# Revit family: LAMP_FIL 70 CORNER OPAL RECESSED
name_source: partatom
category: Luminarias
revit_build: Autodesk Revit 2015 (Build: 20140606_1530(x64)
units: mm (PartAtom-declared; Revit-internal decimal feet)

## types (8) — shared parameters
CRI = 80
Cambio de temperatura de color de luz atenuada = <Ninguno>
Comentarios de tipo = Availability of switching between accessories through visibility parameters when placed in a project.
Dimensions = (303 x 368) x 89 x 70 mm
Fabricante = LAMP
Filtro de color = 16777215
Gear = Electronic
IEE = A++
IFC Clasificación = Light Fixture
Installation instructions = https://www.lamp.es
Insulation class = I
LED Lifetime = 50000 L80 B10
Last update = 12/08/2020
Longitud de línea de emisión = 300 mm
Luminaire type = Indoor - Modular System
Lámpara = LED MID-POWER
MacAdam = 3
Manufacturer URL = http://www.lamp.es
Manufacturer country = Spain
Manufacturer name = LAMP
Material Difusor = LAMP_PC Difusor Opal Fil
Model explanation = Availability of switching between accessories through visibility parameters when placed in a project.
Power Supply = 220-240V 50-60Hz
Product URL = https://www.lamp.es
Product datasheet = https://www.lamp.es
Protection rating = IP42, IK06
Recessed dimensions = (305 x 370) x 78 mm
Type = MID POWER PHILIPS
Weight = 1,50 kg
Ángulo de inclinación = 90,00°

## per-type parameters (varying)
| type | Archivo de red fotométrica | Descripción | Efficacy | Finish | Material Perfil | Modelo | Plum | Power | Product code | UniClass 1.4 Code | UniClass 2.0 Code |
| 1300LM 3000K GREY | 14741103.IES | FIL 70 CORNER OPAL REC 1300 WW GR. | 99 lm/W | Gloss grey | LAMP_Aluminio Perfil Fil GR | F71HCRELOOP830NG | 10 W | 9 W | F71HCRELOOP830NG | F71HCRELOOP830NG | F71HCRELOOP830NG |
| 1300LM 3000K WHITE | 14741100.IES | FIL 70 CORNER OPAL REC 1300 WW WH. | 99 lm/W | Matt white | LAMP_Aluminio Perfil Fil BL | F71HCRELOOP830NW | 10 W | 9 W | F71HCRELOOP830NW | F71HCRELOOP830NW | F71HCRELOOP830NW |
| 1300LM 4000K WHITE | 14740100.IES | FIL 70 CORNER OPAL REC 1300 NW WH. | 104 lm/W | Matt white | LAMP_Aluminio Perfil Fil BL | F71HCRELOOP840NW | 10 W | 9 W | F71HCRELOOP840NW | F71HCRELOOP840NW | F71HCRELOOP840NW |
| 1300LM 4000K GREY | 14740103.IES | FIL 70 CORNER OPAL REC 1300 NW GR. | 104 lm/W | Gloss grey | LAMP_Aluminio Perfil Fil GR | F71HCRELOOP840NG | 10 W | 9 W | F71HCRELOOP840NG | F71HCRELOOP840NG | F71HCRELOOP840NG |
| 2200LM 3000K WHITE | 14741110.IES | FIL 70 CORNER OPAL REC 2200 WW WH. | 105 lm/W | Matt white | LAMP_Aluminio Perfil Fil BL | F71HCREHOOP830NW | 16 W | 14 W | F71HCREHOOP830NW | F71HCREHOOP830NW | F71HCREHOOP830NW |
| 2200LM 3000K GREY | 14741113.IES | FIL 70 CORNER OPAL REC 2200 WW GR. | 105 lm/W | Gloss grey | LAMP_Aluminio Perfil Fil GR | F71HCREHOOP830NG | 16 W | 14 W | F71HCREHOOP830NG | F71HCREHOOP830NG | F71HCREHOOP830NG |
| 2200LM 4000K WHITE | 14740110.IES | FIL 70 CORNER OPAL REC 2200 NW WH. | 113 lm/W | Matt white | LAMP_Aluminio Perfil Fil BL | F71HCREHOOP840NW | 16 W | 14 W | F71HCREHOOP840NW | F71HCREHOOP840NW | F71HCREHOOP840NW |
| 2200LM 4000K GREY | 14740113.IES | FIL 70 CORNER OPAL REC 2200 NW GR. | 113 lm/W | Gloss grey | LAMP_Aluminio Perfil Fil GR | F71HCREHOOP840NG | 16 W | 14 W | F71HCREHOOP840NG | F71HCREHOOP840NG | F71HCREHOOP840NG |

## geometry (parser evidence)
native form markers: Blend x16
no freeform markers — native parametric forms only
